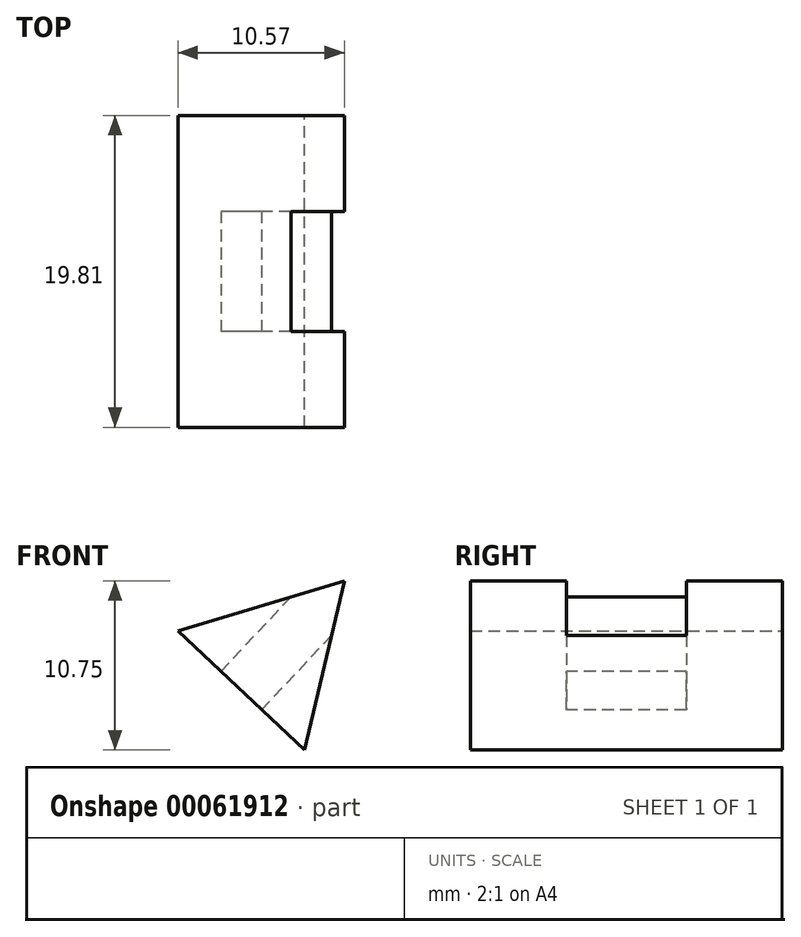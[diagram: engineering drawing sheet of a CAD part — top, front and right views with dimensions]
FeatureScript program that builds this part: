
annotation { "Feature Type Name" : "Feature", "Feature Type Description" : "" }
export const myFeature = defineFeature(function(context is Context, id is Id, definition is map)
    precondition{}
    {
        {
            var Q0;
            Q0=qCreatedBy(makeId("Front.planeOp"),FACE);
            var sketch = newSketch(context, id + "F0", { "sketchPlane" : qUnion([Q0])});
            skLineSegment(sketch, "E0", {"start": v(-36.31, 5.73) * mm, "end": v(-28.26, -1.83) * mm});
            skLineSegment(sketch, "E1", {"start": v(-28.26, -1.83) * mm, "end": v(-25.74, 8.92) * mm});
            skLineSegment(sketch, "E2", {"start": v(-25.74, 8.92) * mm, "end": v(-36.31, 5.73) * mm});
            skSolve(sketch);
        }
        {
            var Q0;
            Q0=makeQuery(id+"F0.imprint","IMPRINT",FACE,{"disambiguationData":[TD([[makeQuery(id+"F0.imprint","IMPRINT",EDGE,{"derivedFrom":sQuery(id+"F0.wireOp",EDGE,"E0")}),1.0]])]});
            extrude(context, id + "F1", {"entities" : qUnion([Q0]), "depth" : 19.8 * mm});
        }
        {
            var Q0;
            Q0=makeQuery(id+"F1.opExtrude","SWEPT_FACE",FACE,{"disambiguationData":[OSD([sQuery(id+"F0.wireOp",EDGE,"E0")])]});
            var sketch = newSketch(context, id + "F2", { "sketchPlane" : qUnion([Q0])});
            skLineSegment(sketch, "E3.bottom", {"start": v(-23.1, 6.1) * mm, "end": v(-26.65, 6.1) * mm});
            skLineSegment(sketch, "E3.top", {"start": v(-23.1, 13.72) * mm, "end": v(-26.65, 13.72) * mm});
            skLineSegment(sketch, "E3.left", {"start": v(-23.1, 6.1) * mm, "end": v(-23.1, 13.72) * mm});
            skLineSegment(sketch, "E3.right", {"start": v(-26.65, 6.1) * mm, "end": v(-26.65, 13.72) * mm});
            skLineSegment(sketch, "E4", {"start": v(-30.4, 9.9) * mm, "end": v(-19.35, 9.9) * mm, "construction": true});
            skLineSegment(sketch, "E5", {"start": v(-24.87, 0) * mm, "end": v(-24.87, 19.81) * mm, "construction": true});
            skSolve(sketch);
        }
        {
            var Q0;
            Q0=makeQuery(id+"F2.imprint","IMPRINT",FACE,{"disambiguationData":[TD([[makeQuery(id+"F2.imprint","IMPRINT",EDGE,{"derivedFrom":sQuery(id+"F2.wireOp",EDGE,"E3.bottom")}),-1.0]])]});
            extrude(context, id + "F3", {"entities" : qUnion([Q0]), "operationType" : NewBodyOperationType.REMOVE, "oppositeDirection" : true, "depth" : 25.4 * mm});
        }
    });
